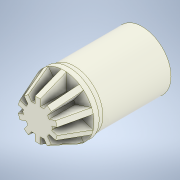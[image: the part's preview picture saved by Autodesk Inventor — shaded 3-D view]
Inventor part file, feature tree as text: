
AUTODESK INVENTOR PART (.ipt)
format: ipt  version: 2022.6 (Build 266554000, 554)  size: 269,824 bytes
history: native  units: mm
features: extrude x6, thicken_offset x2, chamfer x1, hole x1, pattern_circular x1, fillet x1
ambient origin geometry x8: Origin, YZ Plane, XZ Plane, XY Plane, X Axis, Y Axis, Z Axis, Center Point
bodies: Solid1 (feature_tree)
feature tree (12):
  extrude  "Adapter"  Depth=11.0mm
  extrude  "Motor Shaft Profile"  Depth=1.0mm TaperAngle=0.0deg
  chamfer  "Chamfer1"  Distance=13.0mm
  thicken_offset  "Thicken5"
  thicken_offset  "Thicken6"
  hole  "Hole6"  [1 undecoded]
  extrude  "Extrusion5"  Depth=13.0mm TaperAngle=0.0deg
  extrude  "Extrusion6"  Depth=0.2mm
  extrude  "Extrusion7"  Depth=2.0mm TaperAngle=45.0deg
  pattern_circular  "Circular Pattern1"  [2 undecoded]
  extrude  "Extrusion8"  Depth=0.2mm
  fillet  "Fillet1"  Radius=11.5mm
note: 3 required parameter values undecoded (feature->parameter linkage not recoverable at this tier; creation-order binding heuristic only, values carry confidence <= 0.55)
